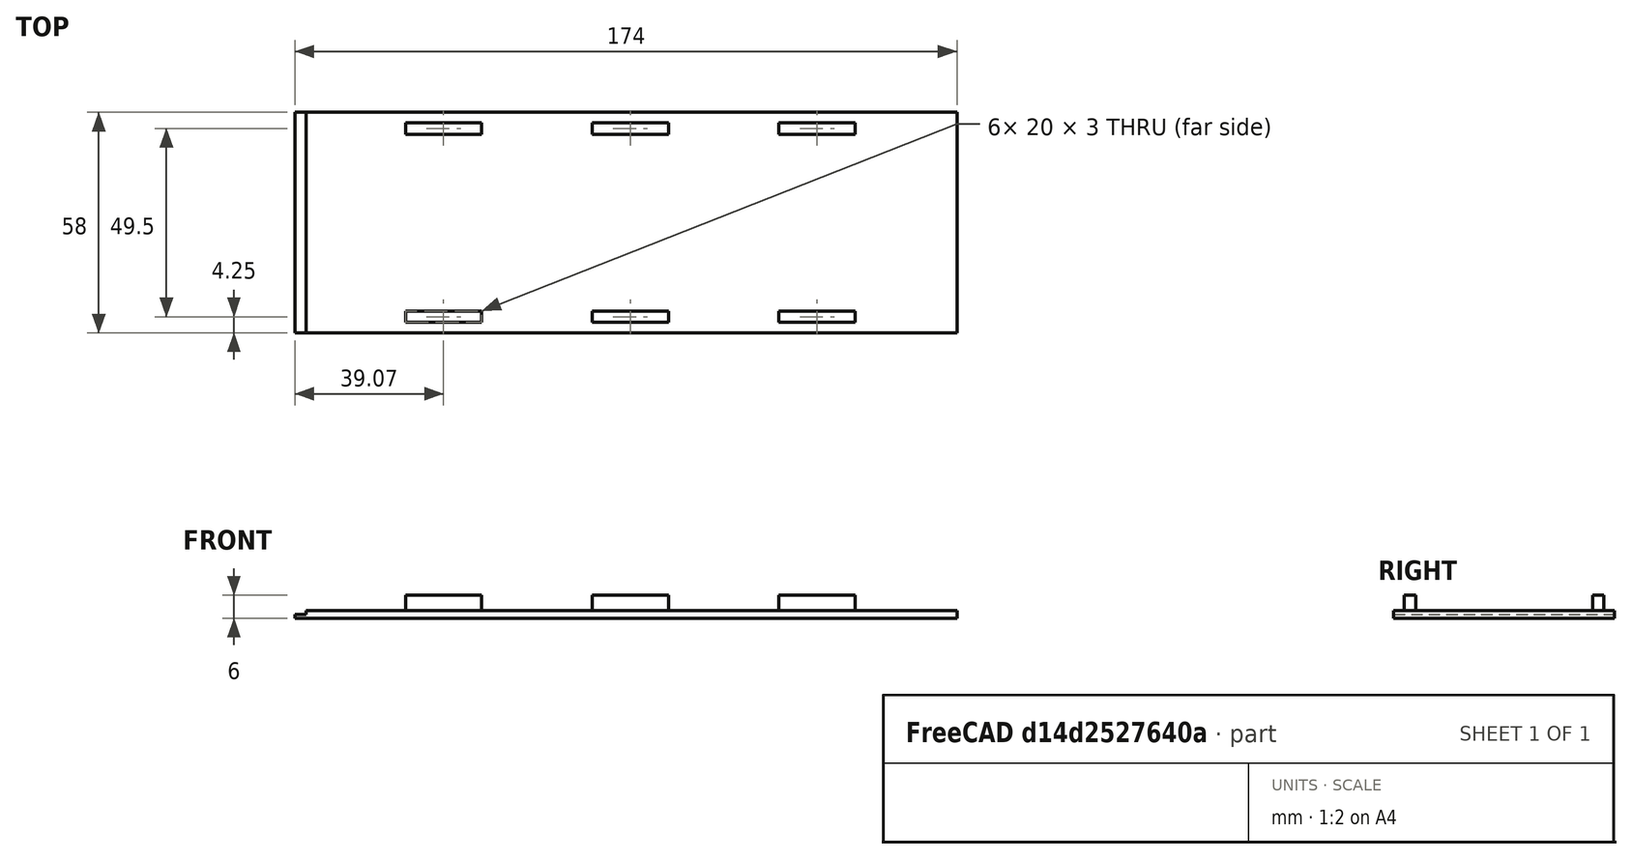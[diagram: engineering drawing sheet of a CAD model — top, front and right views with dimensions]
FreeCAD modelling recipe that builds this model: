
FCSTD DOCUMENT  (FreeCAD 0.21R33694 (Git))
Label: maze_cover_A_v3
License: All rights reserved
LicenseURL: https://en.wikipedia.org/wiki/All_rights_reserved
objects: Part::Box×8, Part::MultiFuse×1
note: 9 computed .brp shape members not serialized (recipe doc carries the construction recipe); baked Part::Feature solids carry a one-line shape summary decoded from their .brp

FEATURE [Part::Box] Box  label="Cube"
  AttacherType = Attacher::AttachEngine3D
  Height = 2
  Length = 171
  Placement = pos=(3,0,0) rot=(0,0,1;0rad)
  Width = 58
FEATURE [Part::Box] Box001  label="Cube001"
  AttacherType = Attacher::AttachEngine3D
  Height = 6
  Length = 20
  Placement = pos=(29.07,2.75,0) rot=(0,0,1;0rad)
  Width = 3
FEATURE [Part::Box] Box002  label="Cube002"
  AttacherType = Attacher::AttachEngine3D
  Height = 6
  Length = 20
  Placement = pos=(78.15,2.75,0) rot=(0,0,1;0rad)
  Width = 3
FEATURE [Part::Box] Box003  label="Cube003"
  AttacherType = Attacher::AttachEngine3D
  Height = 6
  Length = 20
  Placement = pos=(127.22,2.75,0) rot=(0,0,1;0rad)
  Width = 3
FEATURE [Part::Box] Box004  label="Cube004"
  AttacherType = Attacher::AttachEngine3D
  Height = 6
  Length = 20
  Placement = pos=(29.07,52.25,0) rot=(0,0,1;0rad)
  Width = 3
FEATURE [Part::Box] Box005  label="Cube005"
  AttacherType = Attacher::AttachEngine3D
  Height = 6
  Length = 20
  Placement = pos=(78.15,52.25,0) rot=(0,0,1;0rad)
  Width = 3
FEATURE [Part::Box] Box006  label="Cube006"
  AttacherType = Attacher::AttachEngine3D
  Height = 6
  Length = 20
  Placement = pos=(127.22,52.25,0) rot=(0,0,1;0rad)
  Width = 3
FEATURE [Part::Box] Box007  label="Cube007"
  AttacherType = Attacher::AttachEngine3D
  Height = 1
  Length = 3
  Width = 58
FEATURE [Part::MultiFuse] Fusion
  Shapes = -> [Box007,Box006,Box005,Box004,Box003,Box002,Box001,Box]
